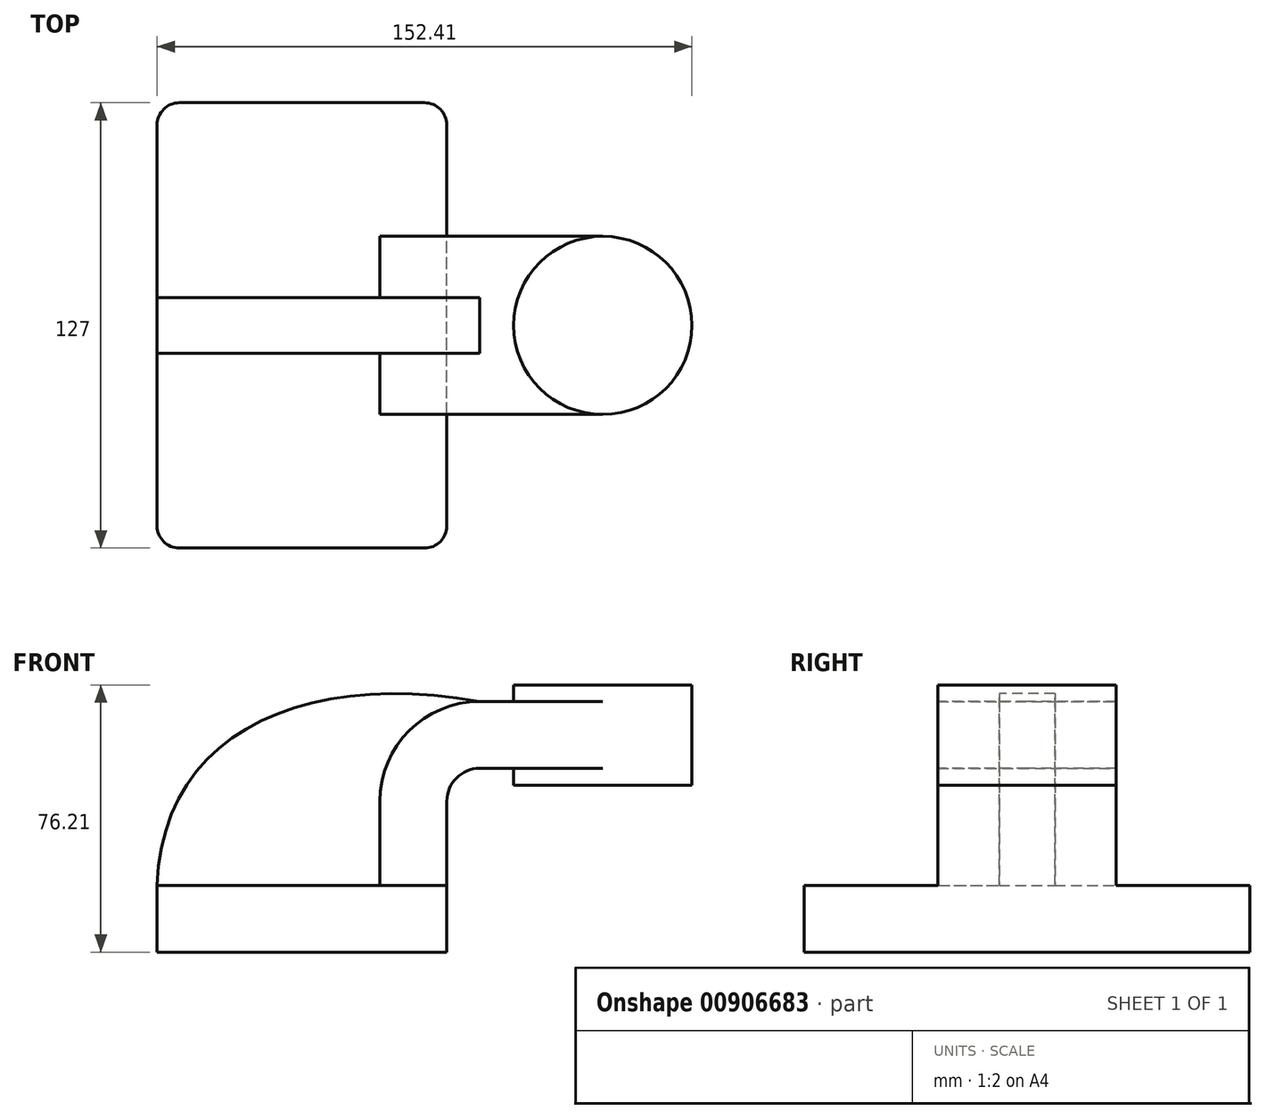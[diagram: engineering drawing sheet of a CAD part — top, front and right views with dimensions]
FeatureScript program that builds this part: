
annotation { "Feature Type Name" : "Feature", "Feature Type Description" : "" }
export const myFeature = defineFeature(function(context is Context, id is Id, definition is map)
    precondition{}
    {
        {
            var Q0;
            Q0=qCreatedBy(makeId("Front.planeOp"),FACE);
            var sketch = newSketch(context, id + "F0", { "sketchPlane" : qUnion([Q0])});
            skLineSegment(sketch, "E0.bottom", {"start": v(-41.28, 9.53) * mm, "end": v(41.28, 9.53) * mm});
            skLineSegment(sketch, "E0.top", {"start": v(-41.28, -9.53) * mm, "end": v(41.28, -9.53) * mm});
            skLineSegment(sketch, "E0.left", {"start": v(-41.28, 9.53) * mm, "end": v(-41.28, -9.53) * mm});
            skLineSegment(sketch, "E0.right", {"start": v(41.28, 9.53) * mm, "end": v(41.28, -9.53) * mm});
            skPoint(sketch, "E0.middle", {"position": v(0, 0) * mm});
            skLineSegment(sketch, "E1", {"start": v(41.28, 33.53) * mm, "end": v(41.28, 9.53) * mm});
            skLineSegment(sketch, "E2.bottom", {"start": v(60.32, 38.1) * mm, "end": v(111.12, 38.1) * mm});
            skLineSegment(sketch, "E2.top", {"start": v(60.32, 66.67) * mm, "end": v(111.12, 66.67) * mm});
            skLineSegment(sketch, "E2.left", {"start": v(60.32, 38.1) * mm, "end": v(60.32, 66.67) * mm});
            skLineSegment(sketch, "E2.right", {"start": v(111.12, 38.1) * mm, "end": v(111.12, 66.67) * mm});
            skPoint(sketch, "E2.middle", {"position": v(85.72, 52.39) * mm});
            skArc(sketch, "E3", {"start": v(41.27, 33.53) * mm, "mid": v(44.01, 40.14) * mm, "end": v(50.62, 42.88) * mm});
            skLineSegment(sketch, "E4", {"start": v(50.62, 42.88) * mm, "end": v(85.72, 42.88) * mm});
            skLineSegment(sketch, "E5.0", {"start": v(22.22, 33.53) * mm, "end": v(22.22, 9.53) * mm});
            skArc(sketch, "E5.1", {"start": v(22.22, 33.53) * mm, "mid": v(30.54, 53.6) * mm, "end": v(50.62, 61.93) * mm});
            skLineSegment(sketch, "E5.2", {"start": v(50.62, 61.93) * mm, "end": v(85.72, 61.93) * mm});
            skLineSegment(sketch, "E6", {"start": v(85.72, 38.1) * mm, "end": v(85.72, 66.67) * mm});
            skFitSpline(sketch, "E7", {"points": [v(-41.28, 9.53) * mm, v(50.62, 61.93) * mm], "startDerivative": vector(4.11, 129.5) * mm, "endDerivative": vector(151.87, -26.98) * mm});
            skSolve(sketch);
        }
        {
            var Q0;
            Q0=makeQuery(id+"F0.imprint","IMPRINT",FACE,{"disambiguationData":[TD([[makeQuery(id+"F0.imprint","IMPRINT",EDGE,{"derivedFrom":sQuery(id+"F0.wireOp",EDGE,"E0.top")}),1.0]])]});
            extrude(context, id + "F1", {"entities" : qUnion([Q0]), "endBound" : BoundingType.SYMMETRIC, "depth" : 127 * mm, "offsetDistance" : 25.4 * mm});
        }
        {
            var Q0;
            {var subQ1=sQuery(id+"F0.wireOp",EDGE,"E1");Q0=makeQuery(id+"F0.imprint","IMPRINT",FACE,{"disambiguationData":[TD([[makeQuery(id+"F0.imprint","IMPRINT",EDGE,{"derivedFrom":subQ1}),-1.0]])]});}
            var Q1;
            {var subQ0=sQuery(id+"F0.wireOp",EDGE,"E4");var subQ1=sQuery(id+"F0.wireOp",EDGE,"E2.left");var subQ2=makeQuery(id+"F0.imprint","INTERSECT",VERTEX,{"derivedFrom":[subQ1,subQ0]});Q1=makeQuery(id+"F0.imprint","IMPRINT",FACE,{"disambiguationData":[TD([[makeQuery(id+"F0.imprint","IMPRINT",EDGE,{"disambiguationData":[TD([[subQ2,-1.0]])],"derivedFrom":subQ1}),-1.0]])]});}
            extrude(context, id + "F2", {"entities" : qUnion([Q0, Q1]), "operationType" : NewBodyOperationType.ADD, "endBound" : BoundingType.SYMMETRIC, "depth" : 50.8 * mm, "offsetDistance" : 25.4 * mm});
        }
        {
            var Q0;
            {var subQ2=sQuery(id+"F0.wireOp",EDGE,"E5.0");Q0=makeQuery(id+"F0.imprint","IMPRINT",FACE,{"disambiguationData":[TD([[makeQuery(id+"F0.imprint","IMPRINT",EDGE,{"derivedFrom":subQ2}),-1.0]])]});}
            extrude(context, id + "F3", {"entities" : qUnion([Q0]), "operationType" : NewBodyOperationType.ADD, "endBound" : BoundingType.SYMMETRIC, "depth" : 15.88 * mm, "offsetDistance" : 25.4 * mm});
        }
        {
            var Q0;
            {var subQ4=sQuery(id+"F0.wireOp",EDGE,"E2.right");Q0=makeQuery(id+"F0.imprint","IMPRINT",FACE,{"disambiguationData":[TD([[makeQuery(id+"F0.imprint","IMPRINT",EDGE,{"derivedFrom":subQ4}),1.0]])]});}
            var Q1;
            Q1=sQuery(id+"F0.wireOp",EDGE,"E6");
            revolve(context, id + "F4", {"operationType" : NewBodyOperationType.ADD, "surfaceOperationType" : NewSurfaceOperationType.NEW, "entities" : qUnion([Q0]), "axis" : qUnion([Q1]), "revolveType" : RevolveType.FULL});
        }
        {
            var Q0;
            Q0=makeQuery(id+"F1.opExtrude","CAP_EDGE",EDGE,{"disambiguationData":[OSD([sQuery(id+"F0.wireOp",EDGE,"E0.right")])],"isStart":true});
            var Q1;
            Q1=makeQuery(id+"F1.opExtrude","CAP_EDGE",EDGE,{"disambiguationData":[OSD([sQuery(id+"F0.wireOp",EDGE,"E0.right")])],"isStart":false});
            var Q2;
            Q2=makeQuery(id+"F1.opExtrude","CAP_EDGE",EDGE,{"disambiguationData":[OSD([sQuery(id+"F0.wireOp",EDGE,"E0.left")])],"isStart":true});
            var Q3;
            Q3=makeQuery(id+"F1.opExtrude","CAP_EDGE",EDGE,{"disambiguationData":[OSD([sQuery(id+"F0.wireOp",EDGE,"E0.left")])],"isStart":false});
            fillet(context, id + "F5", {"entities" : qUnion([Q0, Q1, Q2, Q3]), "radius" : 6.35 * mm, "tangentPropagation" : true, "allowEdgeOverflow" : false});
        }
    });
